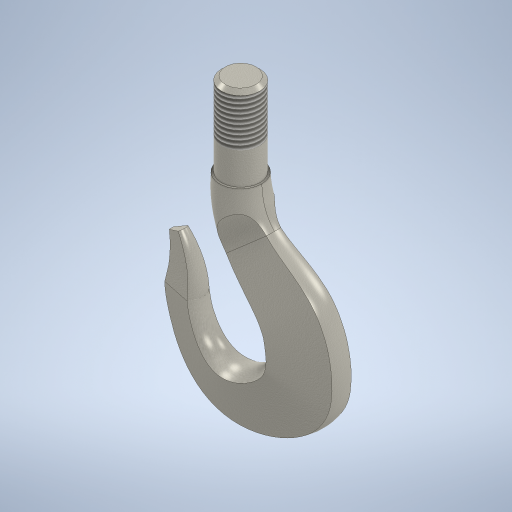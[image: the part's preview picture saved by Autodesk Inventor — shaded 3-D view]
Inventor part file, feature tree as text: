
AUTODESK INVENTOR PART (.ipt)
format: ipt  version: 2024 (Build 280153000, 153)  size: 729,088 bytes
history: native  units: mm
features: other x20, plane x15, loft x3, extrude x2, sketch x2, mirror x1, thread x1, chamfer x1
ambient origin geometry x8: Origin, YZ Plane, XZ Plane, XY Plane, X Axis, Y Axis, Z Axis, Center Point
bodies: Solid1 (feature_tree)
feature tree (45):
  other  "Basic Sketch"
  plane  "Work Plane1"
  plane  "Work Plane2"
  plane  "Work Plane3"
  plane  "Work Plane4"
  plane  "Work Plane5"
  plane  "Work Plane6"
  plane  "Work Plane7"
  plane  "Work Plane8"
  plane  "Work Plane10"
  other  "Section 1"
  loft  "Loft1"
  loft  "Loft2"
  other  "Segment 3"
  plane  "Work Plane11"
  plane  "Work Plane12"
  plane  "Work Plane13"
  plane  "Work Plane14"
  plane  "Work Plane15"
  loft  "Loft3"
  other  "Work Axis1"
  other  "Work Point1"
  plane  "Work Plane16"
  extrude  "Extrusion1"  Depth=25.0mm
  mirror  "Mirror1"
  extrude  "Extrusion2"  Depth=100.0mm
  thread  "Thread1"  [1 undecoded]
  chamfer  "Chamfer1"  Distance=6.0mm
  other  "Section 2"
  other  "Section 5"
  other  "Section 3"
  other  "Section 4"
  other  "Section 6"
  other  "Section 7"
  other  "Section 8"
  other  "Section 9"
  other  "Section 1_0"
  other  "Section 10"
  other  "Section 11"
  other  "Section 12"
  other  "Section 13"
  other  "Section 14"
  other  "Section Start"
  sketch  "Sketch19"  dims[d0=33.0mm d1=100.0mm]
  sketch  "Sketch20"  dims[d2=30.0mm d3=68.0mm d4=12.0mm d5=42.0mm d6=100.0mm d7=62.0mm d8=6.0mm d9=36.0mm d10=21.0mm d11=66.0mm d12=6.981317mm d13=4.363323mm d14=4.363323mm d15=30.0deg d16=6.108652mm d17=90.0deg d18=33.0mm d19=90.0deg d20=90.0deg d21=15.0mm d22=33.0mm d24=4.161261mm d25=37.574812mm d26=24.799376mm d27=90.0deg d28=4.161261mm d29=47.156537mm d30=31.123315mm d31=90.0deg d32=4.161261mm d33=49.307455mm d34=32.54292mm d35=90.0deg d36=4.161261mm d37=48.998428mm d38=32.338962mm d39=90.0deg d40=4.161261mm d41=36.932802mm d42=24.375649mm d43=90.0deg d44=4.161261mm d45=27.820936mm d46=18.361818mm d47=90.0deg d48=4.161261mm d49=26.0mm d50=17.16mm d51=0.0mm d52=90.0deg d53=0.0mm d54=90.0deg d55=0.0mm d56=90.0deg d57=0.0mm d58=90.0deg d59=0.0mm d60=90.0deg d61=0.0mm d62=90.0deg d63=0.0mm d64=90.0deg d65=0.0mm d66=90.0deg d67=0.0mm d68=90.0deg d69=0.0mm d70=90.0deg d71=0.0mm d72=90.0deg d73=0.0mm d74=90.0deg d75=30.0mm d76=15.0deg d77=3.0mm d78=12.0mm d79=20.0mm d80=90.0deg d81=4.161261mm d82=25.295786mm d83=16.695219mm d84=90.0deg d85=4.161261mm d86=22.435744mm d87=14.807591mm d88=90.0deg d89=4.161261mm d90=19.805096mm d91=13.071363mm d92=90.0deg d93=4.161261mm d94=15.339196mm d95=10.123869mm d96=90.0deg d97=4.161261mm d98=11.671766mm d99=7.703366mm d100=0.0mm d101=90.0deg d102=0.0mm d103=90.0deg d104=0.0mm d105=90.0deg d106=0.0mm d107=90.0deg d108=0.0mm d109=90.0deg d110=0.0mm d111=90.0deg d112=25.0mm d113=25.0mm d114=0.0mm d115=0.0mm d116=30.0mm d117=65.0mm d118=0.0mm d119=40.0mm d120=0.0mm d121=3.0mm d122=2.0mm d123=45.0deg]
note: 1 required parameter value undecoded (feature->parameter linkage not recoverable at this tier; creation-order binding heuristic only, values carry confidence <= 0.55)
